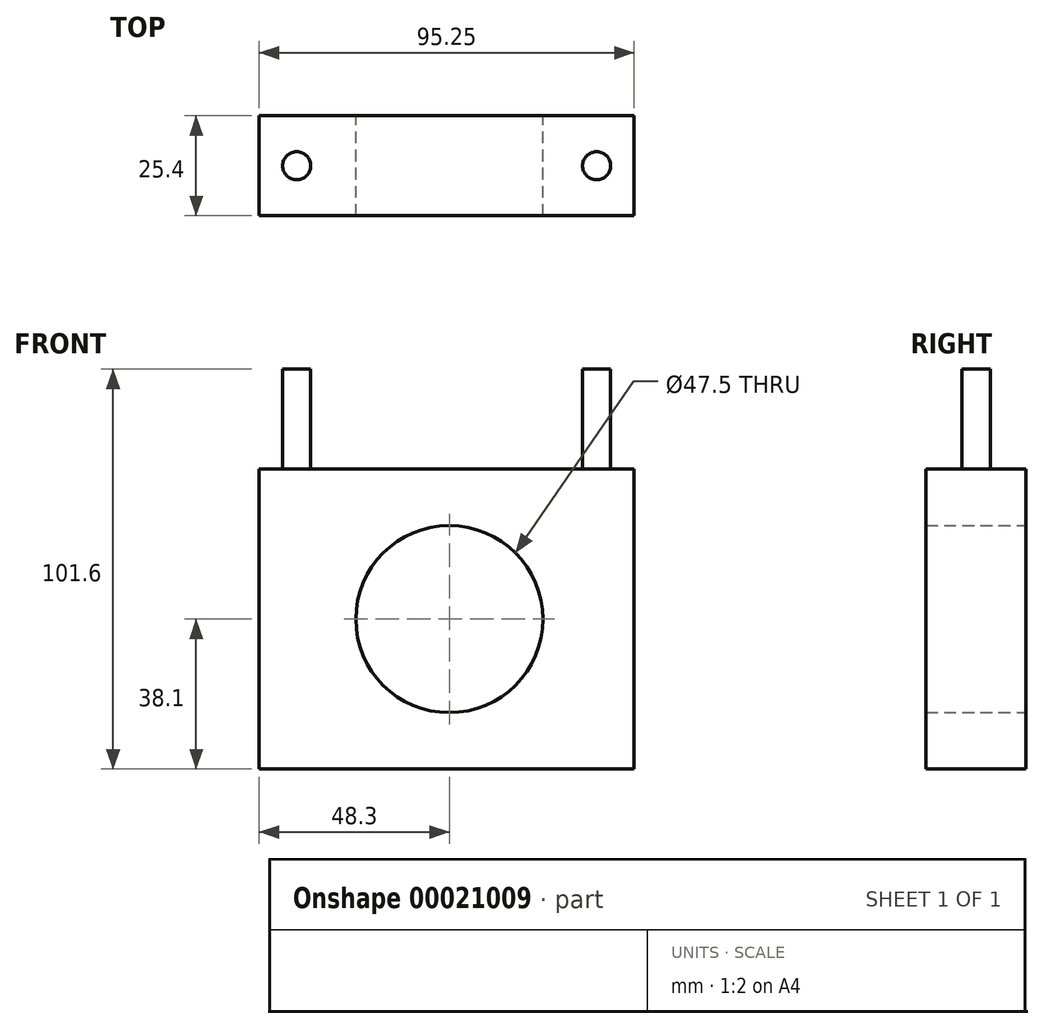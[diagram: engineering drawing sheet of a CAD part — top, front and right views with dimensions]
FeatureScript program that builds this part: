
annotation { "Feature Type Name" : "Feature", "Feature Type Description" : "" }
export const myFeature = defineFeature(function(context is Context, id is Id, definition is map)
    precondition{}
    {
        {
            var Q0;
            Q0=qCreatedBy(makeId("Front.planeOp"),FACE);
            var sketch = newSketch(context, id + "F0", { "sketchPlane" : qUnion([Q0])});
            skLineSegment(sketch, "E0.bottom", {"start": v(-48.3, 25.8) * mm, "end": v(46.95, 25.8) * mm});
            skLineSegment(sketch, "E0.left", {"start": v(-48.3, 25.8) * mm, "end": v(-48.3, -50.4) * mm});
            skLineSegment(sketch, "E0.right", {"start": v(46.95, 25.8) * mm, "end": v(46.95, -50.4) * mm});
            skLineSegment(sketch, "E1", {"start": v(-48.3, -50.4) * mm, "end": v(46.95, -50.4) * mm});
            skLineSegment(sketch, "E2.0", {"start": v(-0.8, 25.8) * mm, "end": v(-0.8, -50.4) * mm, "construction": true});
            skLineSegment(sketch, "E3.0", {"start": v(-48.3, -12.3) * mm, "end": v(46.95, -12.3) * mm, "construction": true});
            skCircle(sketch, "E4", {"center": v(0, -12.3) * mm, "radius": 23.75 * mm});
            skSolve(sketch);
        }
        {
            var Q0;
            Q0=makeQuery(id+"F0.imprint","IMPRINT",FACE,{"disambiguationData":[TD([[makeQuery(id+"F0.imprint","IMPRINT",EDGE,{"derivedFrom":sQuery(id+"F0.wireOp",EDGE,"E0.bottom")}),-1.0]])]});
            extrude(context, id + "F1", {"entities" : qUnion([Q0]), "depth" : 25.4 * mm});
        }
        {
            var Q0;
            Q0=makeQuery(id+"F1.opExtrude","SWEPT_FACE",FACE,{"disambiguationData":[OSD([sQuery(id+"F0.wireOp",EDGE,"E0.bottom")])]});
            var sketch = newSketch(context, id + "F2", { "sketchPlane" : qUnion([Q0])});
            skLineSegment(sketch, "E5.0", {"start": v(-48.3, -12.7) * mm, "end": v(46.95, -12.7) * mm, "construction": true});
            skLineSegment(sketch, "E6.0", {"start": v(-38.78, -25.4) * mm, "end": v(-38.78, 0) * mm, "construction": true});
            skCircle(sketch, "E7", {"center": v(-38.78, -12.7) * mm, "radius": 3.57 * mm});
            skLineSegment(sketch, "E8.0", {"start": v(37.42, -25.4) * mm, "end": v(37.42, 0) * mm, "construction": true});
            skCircle(sketch, "E9", {"center": v(37.42, -12.7) * mm, "radius": 3.57 * mm});
            skSolve(sketch);
        }
        {
            var Q0;
            Q0 = qSketchRegion(id + "F2", true);
            extrude(context, id + "F3", {"entities" : qUnion([Q0]), "operationType" : NewBodyOperationType.ADD, "depth" : 25.4 * mm});
        }
    });
